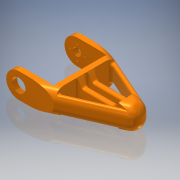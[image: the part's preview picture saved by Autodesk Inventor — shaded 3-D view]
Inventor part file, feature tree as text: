
AUTODESK INVENTOR PART (.ipt)
format: ipt  version: 2017 (Build 210142000, 142)  size: 539,648 bytes
history: native  units: mm
features: extrude x6, sketch x6, fillet x4
ambient origin geometry x8: Origin, YZ Plane, XZ Plane, XY Plane, X Axis, Y Axis, Z Axis, Center Point
bodies: Solid1 (feature_tree)
feature tree (16):
  extrude  "Extrusion1"  Depth=10.0mm
  extrude  "Extrusion8"  TaperAngle=0.0deg  [1 undecoded]
  extrude  "Extrusion9"  Depth=45.5mm
  fillet  "Fillet5"  Radius=5.0mm
  extrude  "Extrusion12"  Depth=5.0mm
  extrude  "Extrusion13"  Depth=10.0mm
  extrude  "Extrusion14"  Depth=10.0mm TaperAngle=0.0deg
  fillet  "Fillet7"  Radius=12.0mm
  fillet  "Fillet8"  Radius=15.0mm
  fillet  "Fillet9"  Radius=5.0mm
  sketch  "Sketch1"  dims[d0=90.0mm d1=10.0mm]
  sketch  "Sketch9"  dims[d2=24.0mm d3=0.0mm]
  sketch  "Sketch10"  dims[d4=61.0mm d68=45.5mm d69=5.0mm]
  sketch  "Sketch15"  dims[d70=5.0mm d71=5.0mm]
  sketch  "Sketch16"  dims[d72=10.0mm d73=0.0mm d74=5.0mm]
  sketch  "Sketch17"  dims[d75=5.0mm d77=10.0mm d78=0.0mm d80=12.0mm d81=15.0mm d82=5.0mm d95=13.0mm d96=10.0mm d97=0.0mm d98=7.7mm d99=2.0mm d100=7.0mm d101=7.0mm d102=7.0mm d103=7.0mm d104=10.0mm d105=0.0mm d106=60.0deg d107=60.0deg d108=60.0deg d109=60.0deg d110=10.0mm d111=10.0mm d112=0.0mm d113=10.0mm d115=2.0mm d116=1.0mm]
note: 1 required parameter value undecoded (feature->parameter linkage not recoverable at this tier; creation-order binding heuristic only, values carry confidence <= 0.55)
